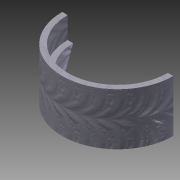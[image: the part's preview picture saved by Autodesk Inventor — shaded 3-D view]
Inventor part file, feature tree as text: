
AUTODESK INVENTOR PART (.ipt)
format: ipt  version: 2015 (Build 190159000, 159)  size: 128,000 bytes
history: native  units: in
note: dims shown in document units (in); Inventor stores cm internally (conversion verified against a paired STEP export)
features: revolve x1, sketch x1
ambient origin geometry x8: Origin, YZ Plane, XZ Plane, XY Plane, X Axis, Y Axis, Z Axis, Center Point
bodies: Solid1 (feature_tree)
feature tree (2):
  revolve  "Revolution1"  [1 undecoded]
  sketch  "Sketch1"  dims[d0=0.75in d1=1.0in d2=0.2185in d3=2.594in d4=0.5841in d5=0.5in d6=1.844in d7=0.5in d8=1.75in d9=0.25in d10=105.0deg d11=0.5in d12=0.5in d13=0.25in d14=0.375in d15=2.0in d16=0.5in d17=0.25in d18=0.234in d19=0.25in d20=2.0in d21=0.25in d22=105.0deg d23=0.125in d24=0.25in d25=2.3995in d26=0.125in d27=0.25in d28=180.0deg]
note: 1 required parameter value undecoded (feature->parameter linkage not recoverable at this tier; creation-order binding heuristic only, values carry confidence <= 0.55)
